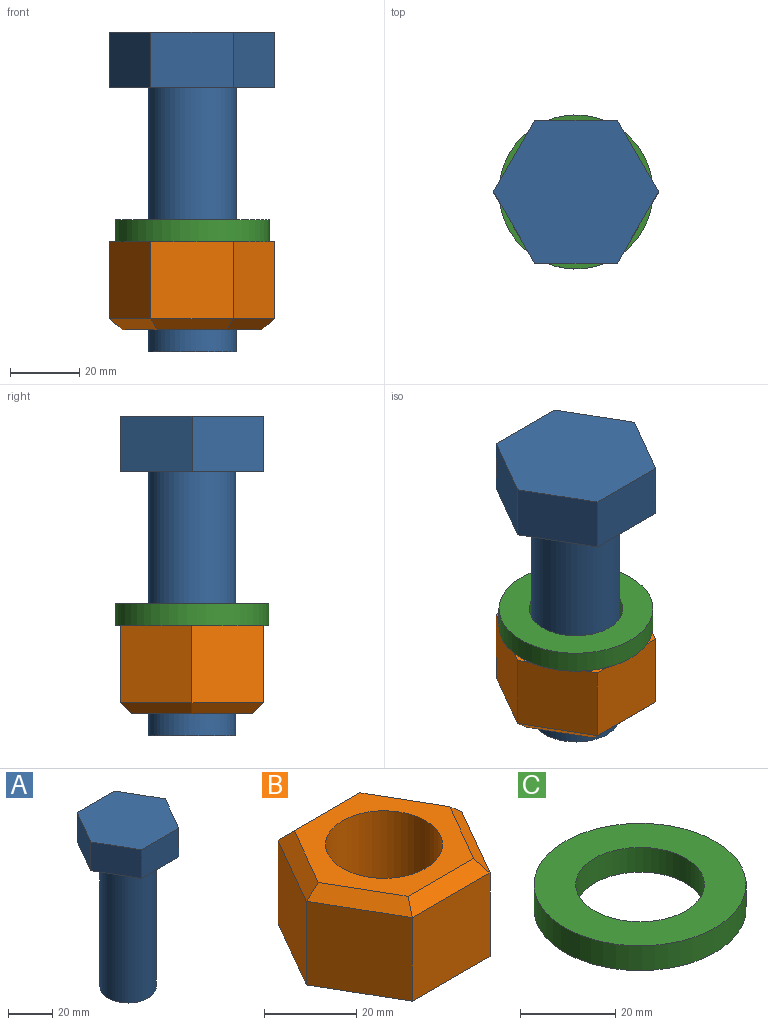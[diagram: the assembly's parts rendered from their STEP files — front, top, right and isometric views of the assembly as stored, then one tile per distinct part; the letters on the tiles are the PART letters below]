
ASSEMBLY  parts=3 mates=2
PART A: 10 faces, bbox 47.7x41.3x92.1 mm
  f0: cylinder r=12.7mm len=76.2mm, axis (0,0,1), area 6080.5mm2, adj f1,f9
  f1: plane 25.4x25.4mm, normal (0,0,-1), area 506.7mm2, adj f0
  f2: plane 20.64x15.88mm, normal (-0.87,0.5,0), area 378.3mm2, adj f3,f7,f8,f9
  f3: plane 20.64x15.88mm, normal (-0.87,-0.5,0), area 378.3mm2, adj f2,f4,f8,f9
  f4: plane 23.83x15.88mm, normal (0,-1,0), area 378.3mm2, adj f3,f5,f8,f9
  f5: plane 20.64x15.88mm, normal (0.87,-0.5,0), area 378.3mm2, adj f4,f6,f8,f9
  f6: plane 20.64x15.88mm, normal (0.87,0.5,0), area 378.3mm2, adj f5,f7,f8,f9
  f7: plane 23.83x15.88mm, normal (0,1,0), area 378.3mm2, adj f2,f6,f8,f9
  f8: plane 47.66x41.28mm, normal (0,0,1), area 1475.4mm2, adj f2,f3,f4,f5,f6,f7
  f9: plane 47.66x41.28mm, normal (0,0,-1), area 968.7mm2, adj f0,f2,f3,f4,f5,f6,f7
PART B: 15 faces, bbox 47.7x41.3x25.4 mm
  f0: plane 22.23x20.64mm, normal (-0.87,0.5,0), area 529.6mm2, adj f1,f6,f8,f9
  f1: plane 22.23x20.64mm, normal (-0.87,-0.5,0), area 529.6mm2, adj f0,f2,f8,f11
  f2: plane 23.83x22.23mm, normal (0,-1,0), area 529.6mm2, adj f1,f3,f8,f13
  f3: plane 22.23x20.64mm, normal (0.87,-0.5,0), area 529.6mm2, adj f2,f4,f8,f14
  f4: plane 22.23x20.64mm, normal (0.87,0.5,0), area 529.6mm2, adj f3,f6,f8,f12
  f5: cylinder r=12.7mm len=25.4mm, axis (0,0,-1), area 2026.8mm2, adj f7,f8
  f6: plane 23.83x22.23mm, normal (0,1,0), area 529.6mm2, adj f0,f4,f8,f10
  f7: plane 40.33x34.93mm, normal (0,0,1), area 549.6mm2, adj f5,f9,f10,f11,f12,f13,f14
  f8: plane 47.66x41.28mm, normal (0,0,-1), area 968.7mm2, adj f0,f1,f2,f3,f4,f5,f6
  f9: plane 20.64x13.75mm, normal (-0.61,0.35,0.71), area 98.8mm2, adj f0,f7,f10,f11
  f10: plane 23.83x3.18mm, normal (0,0.71,0.71), area 98.8mm2, adj f6,f7,f9,f12
  f11: plane 20.64x13.75mm, normal (-0.61,-0.35,0.71), area 98.8mm2, adj f1,f7,f9,f13
  f12: plane 20.64x13.75mm, normal (0.61,0.35,0.71), area 98.8mm2, adj f4,f7,f10,f14
  f13: plane 23.83x3.18mm, normal (0,-0.71,0.71), area 98.8mm2, adj f2,f7,f11,f14
  f14: plane 20.64x13.75mm, normal (0.61,-0.35,0.71), area 98.8mm2, adj f3,f7,f12,f13
PART C: 4 faces, bbox 44.5x44.5x6.4 mm
  f0: cylinder r=13.49mm len=26.99mm, axis (0,0,-1), area 538.4mm2, adj f2,f3
  f1: cylinder r=22.23mm len=44.45mm, axis (0,0,-1), area 886.7mm2, adj f2,f3
  f2: plane 44.45x44.45mm, normal (0,0,1), area 979.8mm2, adj f0,f1
  f3: plane 44.45x44.45mm, normal (0,0,-1), area 979.8mm2, adj f0,f1
PLACE A t=(10.69,28.61,24.92)mm
PLACE B rot(axis=(1,0,0),180deg) t=(10.69,28.61,31.27)mm
PLACE C t=(10.69,28.61,31.27)mm
MATE fastened A.f0 <-> C.f0  axis (0,0,1) through (10.69,28.61,75.72)mm
MATE fastened B.f5 <-> C.f0  axis (0,0,1) through (10.69,28.61,31.27)mm
